# Revit family: 1224xxx Atelier Wall Grande (UL)
name_source: partatom
category: Lighting Fixtures
revit_build: Autodesk Revit 2018 (Build: 20170223_1515(x64)
units: mm (PartAtom-declared; Revit-internal decimal feet)

## family parameters
Always vertical = Yes
Cut with Voids When Loaded = No
Host = Wall
Light Source = No
OmniClass Number = 23.80.70.00
OmniClass Title = Lighting
Part Type = Normal
Room Calculation Point = No
Round Connector Dimension = Use Diameter
Shared = No

## types (3) — shared parameters
ADA compliant = Yes
Dimmable = Not Applicable
Dimming Method = Not Applicable
Driver Included = Not Applicable
Driver Required = No
Efficacy (lm/w) = Lamp Dependent
Electrical Class = 1
Lamp = Incandescent
Light Source Fixed = No
Location / IP Rating = Dry
Main Material = Metal - Aluminium
Manufacturer = Astro Lighting Ltd
Manufacturer URL - Europe and Rest of World = www.astrolighting.com
Manufacturer URL - North America = us.astrolighting.com
Power (Watts) = Lamp Dependent
Product CCT = Lamp Dependent
Product CRI = Lamp Dependent
Product Dimensions (MM) = 430x122x430
Product Location = Indoor
Product Name = Atelier Grande Wall
Product URL = https://us.astrolighting.com
Product Weight (KG) = 0.936
URL = www.astrolighting.com

## per-type parameters (varying)
| type | Main Finish | Product SKU |
| Astro Atelier Grande Wall Polished Aluminium | Polished Aluminium | 1224044 |
| Astro Atelier Grande Wall Matt Black | Matt Black | 1224046 |
| Astro Atelier Grande Wall Matt White | Matt White | 1224045 |

## geometry (parser evidence)
native form markers: Sweep x2
no freeform markers — native parametric forms only
